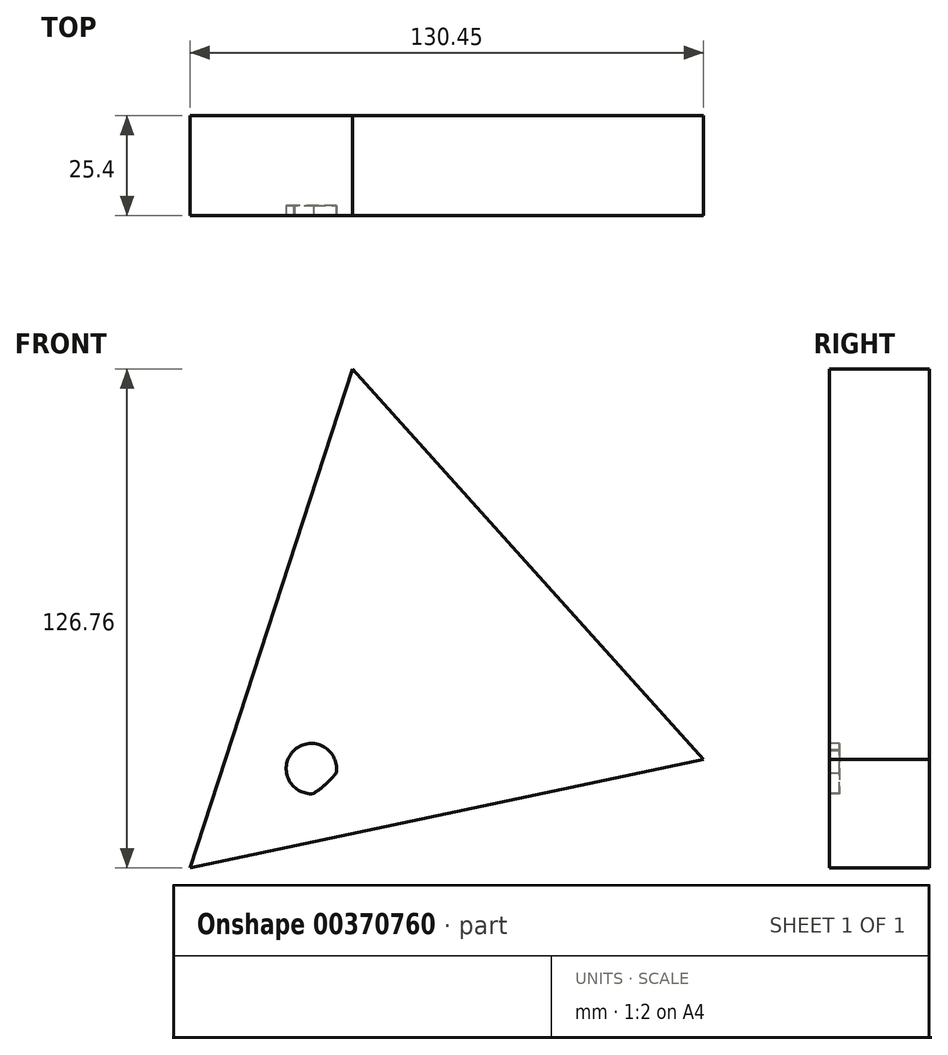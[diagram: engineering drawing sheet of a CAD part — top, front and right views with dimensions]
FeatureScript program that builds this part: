
annotation { "Feature Type Name" : "Feature", "Feature Type Description" : "" }
export const myFeature = defineFeature(function(context is Context, id is Id, definition is map)
    precondition{}
    {
        {
            var Q0;
            Q0=qCreatedBy(makeId("Front.planeOp"),FACE);
            var sketch = newSketch(context, id + "F0", { "sketchPlane" : qUnion([Q0])});
            skCircle(sketch, "E0.cCircle", {"center": v(-214.74, 0) * mm, "radius": 38.49 * mm, "construction": true});
            skLineSegment(sketch, "E0.0", {"start": v(-230.66, 75.31) * mm, "end": v(-141.55, -23.87) * mm});
            skLineSegment(sketch, "E0.1", {"start": v(-141.55, -23.87) * mm, "end": v(-272, -51.45) * mm});
            skLineSegment(sketch, "E0.2", {"start": v(-272, -51.45) * mm, "end": v(-230.66, 75.31) * mm});
            skPoint(sketch, "E0.0.midPoint", {"position": v(-186.1, 25.72) * mm});
            skSolve(sketch);
        }
        {
            var Q0;
            Q0 = qSketchRegion(id + "F0", true);
            extrude(context, id + "F1", {"entities" : qUnion([Q0]), "depth" : 25.4 * mm});
        }
        {
            var Q0;
            Q0=makeQuery(id+"F1.opExtrude","CAP_FACE",FACE,{"disambiguationData":[OSD([sQuery(id+"F0.wireOp",EDGE,"E0.0"),sQuery(id+"F0.wireOp",EDGE,"E0.1"),sQuery(id+"F0.wireOp",EDGE,"E0.2")])],"isStart":false});
            var sketch = newSketch(context, id + "F2", { "sketchPlane" : qUnion([Q0])});
            skCircle(sketch, "E1", {"center": v(-241.18, -26.2) * mm, "radius": 11.86 * mm});
            skCircle(sketch, "E2", {"center": v(-241.18, -26.2) * mm, "radius": 6.39 * mm});
            skFitSpline(sketch, "E3.trimOffspring", {"points": [v(-249.3, -34.85) * mm, v(-236.97, -29.62) * mm, v(-231.85, -18.88) * mm, v(-245.53, -21.53) * mm, v(-249.3, -34.85) * mm]});
            skCircle(sketch, "E4", {"center": v(-241.18, -26.2) * mm, "radius": 2.14 * mm});
            skSolve(sketch);
        }
        {
            var Q0;
            {var subQ1=sQuery(id+"F2.wireOp",EDGE,"E1");var subQ4=makeQuery(id+"F2.imprint","IMPRINT",VERTEX,{"disambiguationData":[OD(0.0)],"derivedFrom":subQ1});Q0=makeQuery(id+"F2.imprint","IMPRINT",FACE,{"disambiguationData":[TD([[makeQuery(id+"F2.imprint","IMPRINT",EDGE,{"disambiguationData":[TD([[subQ4,-1.0]])],"derivedFrom":subQ1}),1.0]])]});}
            var Q1;
            Q1=makeQuery(id+"F2.imprint","IMPRINT",FACE,{"disambiguationData":[TD([[makeQuery(id+"F2.imprint","IMPRINT",EDGE,{"derivedFrom":sQuery(id+"F2.wireOp",EDGE,"E4")}),-1.0]])]});
            var Q2;
            Q2=makeQuery(id+"F2.imprint","IMPRINT",FACE,{"disambiguationData":[TD([[makeQuery(id+"F2.imprint","IMPRINT",EDGE,{"derivedFrom":sQuery(id+"F2.wireOp",EDGE,"E4")}),1.0]])]});
            extrude(context, id + "F3", {"entities" : qUnion([Q0, Q1, Q2]), "operationType" : NewBodyOperationType.REMOVE, "oppositeDirection" : true, "depth" : 2.54 * mm});
        }
    });
